# Revit family: QF_BOURGEAT_Meubles_serviteurs
name_source: partatom
category: Equipement spécialisé
revit_build: Autodesk Revit 2015 (Build: 20140606_1530(x64)
units: mm (PartAtom-declared; Revit-internal decimal feet)

## types (5) — shared parameters
Charge max = 70.00 kg
Fabricant = BOURGEAT
Finition noir = Peinture Grise
Hauteur hors tout = 900 mm
Inox = Acier inoxydable, poli
Longueur hors tout = 540 mm
Profondeur hors tout = 830 mm
Spécification du Fabricant = Meuble serviteur
URL catalogue = http://www.bourgeat.fr

## per-type parameters (varying)
| type | Capacité | Fréquence | Habillage arrière | Indice de protection | Intensité nominale | Modèle | Neutre | Phase | Poids net à vide | Poids à vide | Pour couverts | Pour plateaux | Puissance électrique  | Tension | assiettes chauffant | assiettes neutre |
| Pour assiettes Neutre | 60 assiettes | 0 Hz | Oui |  | 0 A | 859520 | Non | 0 | 42.00 kg | 42 kg | Non | Oui | 0 W | 0 V | Non | Oui |
| Pour assiettes Chauffant | 60 assiettes | 50 Hz | Oui | 21 | 4 A | 859525 | Non | 2 | 44.00 kg | 44 kg | Non | Oui | 900 W | 230 V | Oui | Oui |
| Pour plateaux | 160 plateaux | 0 Hz | Oui |  | 0 A | 859510 | Non | 0 | 23.00 kg | 23 kg | Non | Oui | 0 W | 0 V | Non | Non |
| Pour couverts | 160 plateaux | 0 Hz | Oui |  | 0 A | 859513 | Non | 0 | 32.00 kg | 32 kg | Oui | Non | 0 W | 0 V | Non | Non |
| Neutre | 2 étagères | 0 Hz | Non |  | 0 A | 859505 | Oui | 0 | 29.00 kg | 29 kg | Non | Oui | 0 W | 0 V | Non | Non |

## geometry (parser evidence)
native form markers: Blend x2
no freeform markers — native parametric forms only
